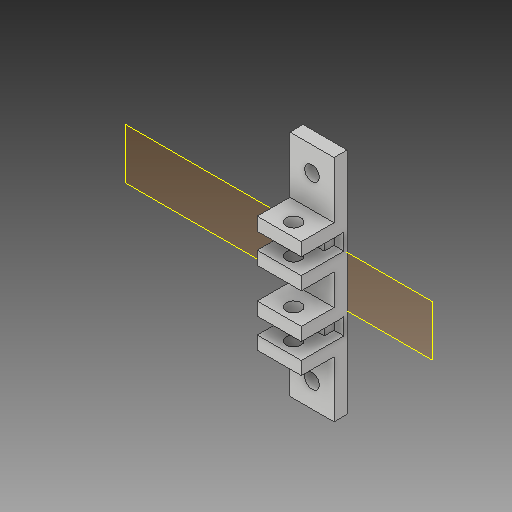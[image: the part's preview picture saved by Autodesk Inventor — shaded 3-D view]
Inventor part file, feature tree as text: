
AUTODESK INVENTOR PART (.ipt)
format: ipt  version: 2017 (Build 210142000, 142)  size: 173,056 bytes
history: native  units: mm
features: other x7, extrude x4, sketch x4, projected_geometry x2
ambient origin geometry x8: Origin, YZ Plane, XZ Plane, XY Plane, X Axis, Y Axis, Z Axis, Center Point
bodies: Solide1 (feature_tree)
feature tree (17):
  other  "Plan de construction1"
  extrude  "Extrusion1"  Depth=4.0mm TaperAngle=0.0deg
  extrude  "Extrusion2"  Depth=4.0mm
  extrude  "Extrusion3"  Depth=5.0mm
  extrude  "Extrusion4"  Depth=4.0mm
  sketch  "Esquisse1"
  other  "Référence1"
  sketch  "Esquisse2"
  other  "Référence2"
  sketch  "Esquisse3"
  sketch  "Esquisse4"
  projected_geometry  "Boucle projetée1"
  projected_geometry  "Boucle projetée2"
  other  "<userpath>\Documents\Modele 3D\Lanceur boule\Ensemble_Lanceur.iam"
  other  "Ensemble_Lanceur.iam"
  other  "aret:1"
  other  "cremaillere:1"
